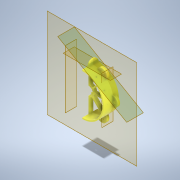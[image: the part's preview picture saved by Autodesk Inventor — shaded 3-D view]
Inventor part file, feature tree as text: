
AUTODESK INVENTOR PART (.ipt)
format: ipt  version: 2021.3 (Build 253353010, 353A)  size: 632,832 bytes
history: native  units: in
note: dims shown in document units (in); Inventor stores cm internally (conversion verified against a paired STEP export)
features: extrude x13, sketch x13, plane x5, pattern_circular x4, fillet x2, mirror x2
ambient origin geometry x8: Origin, YZ Plane, XZ Plane, XY Plane, X Axis, Y Axis, Z Axis, Center Point
bodies: Solid1 (feature_tree)
feature tree (39):
  extrude  "Extrusion1"  Depth=4.25in
  plane  "Work Plane1"
  plane  "Work Plane2"
  extrude  "Extrusion3"  Depth=1.5in
  fillet  "Fillet1"  Radius=2.125in
  extrude  "Extrusion4"  TaperAngle=0.0deg  [1 undecoded]
  pattern_circular  "Circular Pattern2"  Count=2 Angle=360.0deg
  plane  "Work Plane3"
  extrude  "Extrusion5"  Depth=1.0in
  extrude  "Extrusion6"  Depth=0.5in
  fillet  "Fillet2"  [1 undecoded]
  extrude  "Extrusion7"  Depth=0.5in TaperAngle=0.0deg
  pattern_circular  "Circular Pattern3"  [2 undecoded]
  plane  "Work Plane4"
  extrude  "Extrusion8"  Depth=0.5in TaperAngle=0.0deg
  extrude  "Extrusion9"  Depth=0.5in TaperAngle=360.0deg
  extrude  "Extrusion10"  Depth=0.25in
  extrude  "Extrusion11"  Depth=0.125in
  mirror  "Mirror1"
  extrude  "Extrusion12"  Depth=0.25in
  plane  "Work Plane5"
  extrude  "Extrusion13"  Depth=0.2in
  pattern_circular  "Circular Pattern5"  [2 undecoded]
  mirror  "Mirror2"
  extrude  "Extrusion14"  Depth=0.25in
  pattern_circular  "Circular Pattern6"  [2 undecoded]
  sketch  "Sketch1"  dims[d0=4.0in d1=4.25in]
  sketch  "Sketch3"  dims[d2=1.0in d3=0.0in d4=1.5in d10=2.125in]
  sketch  "Sketch4"  dims[d11=0.25in d12=0.0in]
  sketch  "Sketch5"  dims[d13=0.5in d14=0.0in]
  sketch  "Sketch6"  dims[d15=0.5in]
  sketch  "Sketch7"  dims[d16=0.125in]
  sketch  "Sketch10"  dims[d17=0.2in]
  sketch  "Sketch11"  dims[d18=0.5in d19=0.0in d20=0.7874in d21=360.0deg]
  sketch  "Sketch12"  dims[d23=-2.125in d24=1.0in]
  sketch  "Sketch13"  dims[d25=0.25in d26=0.5in d27=0.0in]
  sketch  "Sketch14"  dims[d28=0.1in d29=0.0in d30=0.5in d31=0.0in]
  sketch  "Sketch15"  dims[d32=0.5in]
  sketch  "Sketch16"  dims[d33=0.25in d34=0.2in d35=0.5in d36=0.0in d37=2.3622in d38=360.0deg d40=0.25in d41=0.125in d42=0.25in d43=0.2in d54=0.5312in d55=0.25in d56=4.0in d57=4.0in d58=45.0deg d59=0.125in d60=4.0in d61=135.0deg d62=0.125in d63=4.0in d64=0.0in d65=0.125in d66=0.8661in d67=1.0236in d68=0.3543in d69=0.0in d70=0.5512in d71=0.0787in d72=0.0in d75=0.45in d76=0.2in d77=0.0in d81=0.1in d82=0.0in d83=0.5in d84=0.0in d85=90.0deg d86=0.125in d87=0.675in d88=0.3375in d91=0.1416in d92=0.1416in d93=0.5in d94=0.0in d95=1.9685in d96=120.0deg d98=0.0in d99=0.0in d100=2.3622in d101=360.0deg d53=0.0344in]
note: 8 required parameter values undecoded (feature->parameter linkage not recoverable at this tier; creation-order binding heuristic only, values carry confidence <= 0.55)
